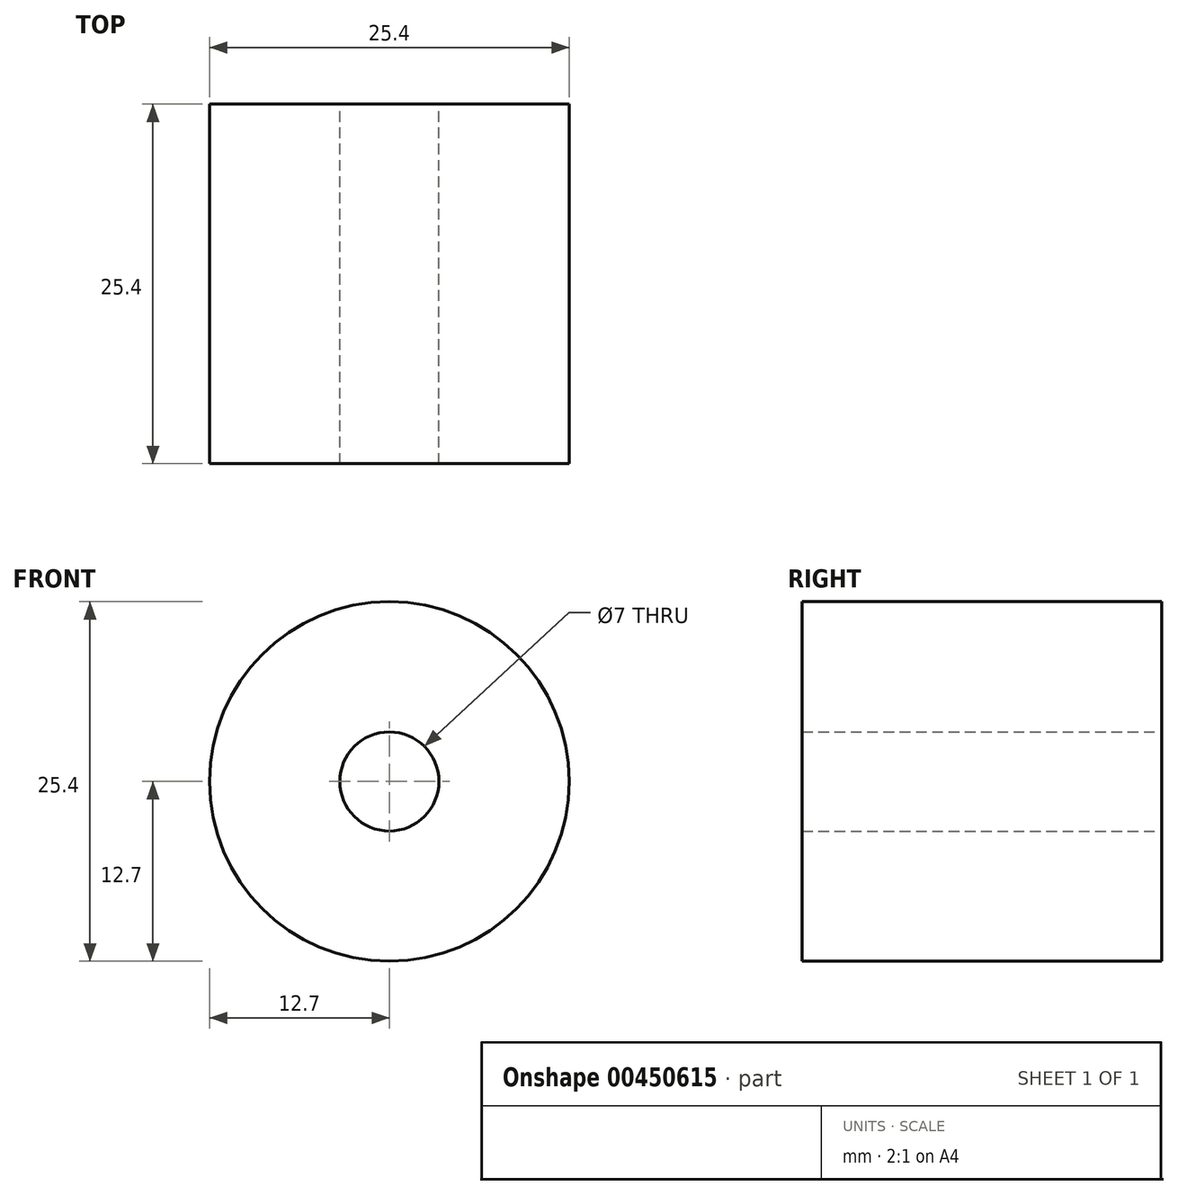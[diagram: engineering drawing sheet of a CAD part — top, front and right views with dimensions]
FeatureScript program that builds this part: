
annotation { "Feature Type Name" : "Feature", "Feature Type Description" : "" }
export const myFeature = defineFeature(function(context is Context, id is Id, definition is map)
    precondition{}
    {
        {
            var Q0;
            Q0=qCreatedBy(makeId("Front.planeOp"),FACE);
            var sketch = newSketch(context, id + "F0", { "sketchPlane" : qUnion([Q0])});
            skCircle(sketch, "E0", {"center": v(0, 0) * mm, "radius": 12.7 * mm});
            skCircle(sketch, "E1", {"center": v(0, 0) * mm, "radius": 3.5 * mm});
            skSolve(sketch);
        }
        {
            var Q0;
            Q0=makeQuery(id+"F0.imprint","IMPRINT",FACE,{"disambiguationData":[TD([[makeQuery(id+"F0.imprint","IMPRINT",EDGE,{"derivedFrom":sQuery(id+"F0.wireOp",EDGE,"E0")}),1.0]])]});
            extrude(context, id + "F1", {"entities" : qUnion([Q0]), "depth" : 25.4 * mm});
        }
    });
